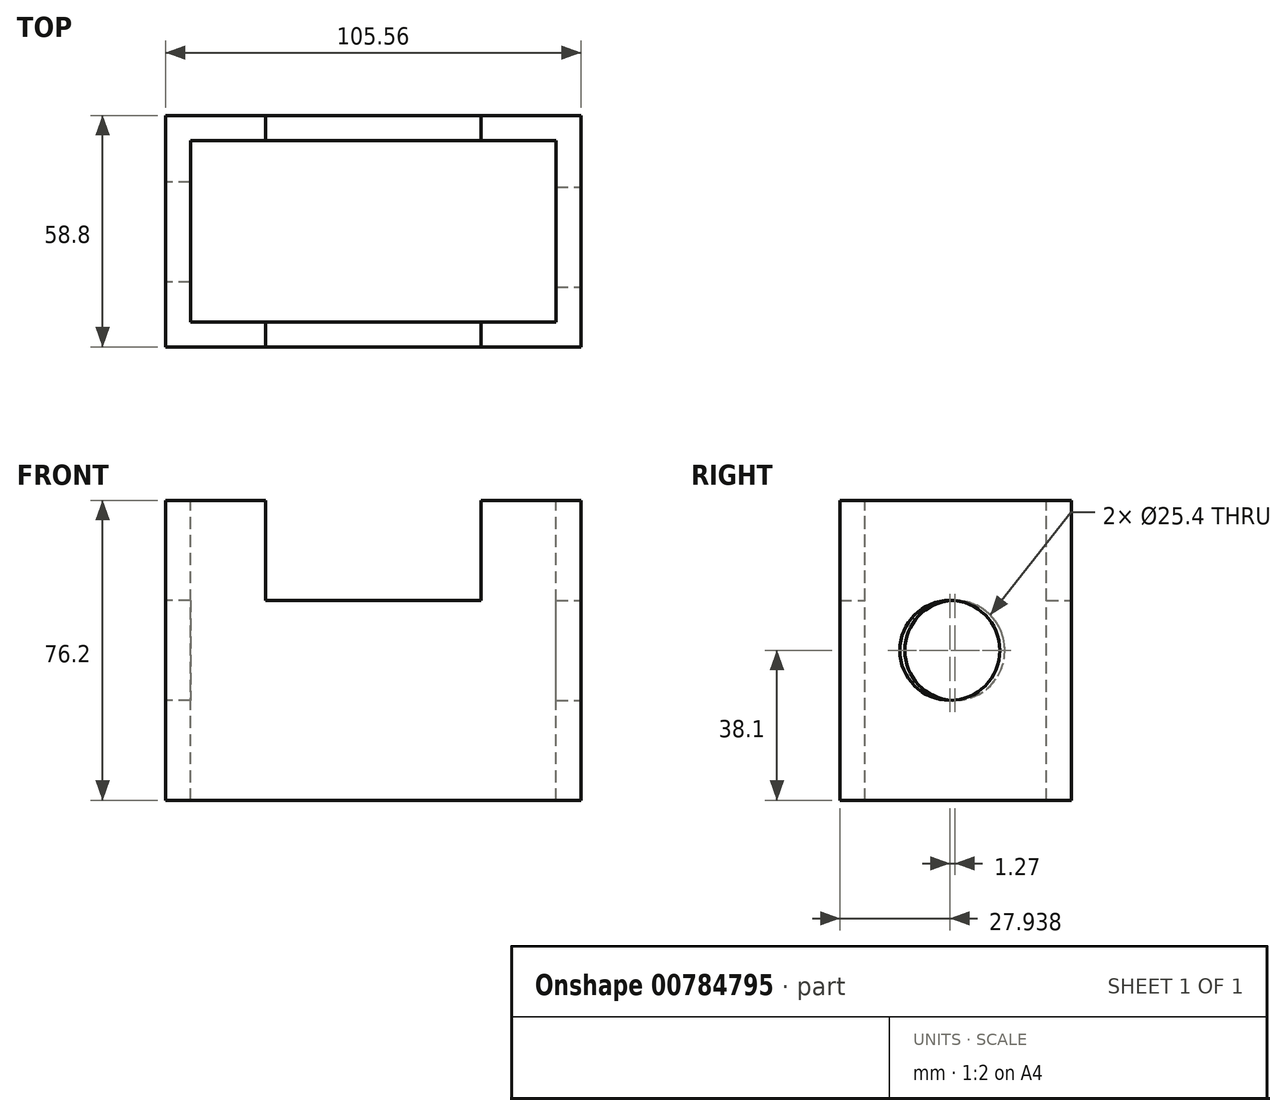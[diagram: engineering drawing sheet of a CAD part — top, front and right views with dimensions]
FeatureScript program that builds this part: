
annotation { "Feature Type Name" : "Feature", "Feature Type Description" : "" }
export const myFeature = defineFeature(function(context is Context, id is Id, definition is map)
    precondition{}
    {
        {
            var Q0;
            Q0=qCreatedBy(makeId("Top.planeOp"),FACE);
            var sketch = newSketch(context, id + "F0", { "sketchPlane" : qUnion([Q0])});
            skLineSegment(sketch, "E0.bottom", {"start": v(-50.25, 19.4) * mm, "end": v(55.3, 19.4) * mm});
            skLineSegment(sketch, "E0.top", {"start": v(-50.25, -39.4) * mm, "end": v(55.3, -39.4) * mm});
            skLineSegment(sketch, "E0.left", {"start": v(-50.25, 19.4) * mm, "end": v(-50.25, -39.4) * mm});
            skLineSegment(sketch, "E0.right", {"start": v(55.3, 19.4) * mm, "end": v(55.3, -39.4) * mm});
            skSolve(sketch);
        }
        {
            var Q0;
            Q0=makeQuery(id+"F0.imprint","IMPRINT",FACE,{"disambiguationData":[TD([[makeQuery(id+"F0.imprint","IMPRINT",EDGE,{"derivedFrom":sQuery(id+"F0.wireOp",EDGE,"E0.bottom")}),-1.0]])]});
            extrude(context, id + "F1", {"entities" : qUnion([Q0]), "depth" : 76.2 * mm, "offsetDistance" : 25.4 * mm});
        }
        {
            var Q0;
            Q0=makeQuery(id+"F1.opExtrude","CAP_FACE",FACE,{"disambiguationData":[OSD([sQuery(id+"F0.wireOp",EDGE,"E0.bottom"),sQuery(id+"F0.wireOp",EDGE,"E0.top"),sQuery(id+"F0.wireOp",EDGE,"E0.left"),sQuery(id+"F0.wireOp",EDGE,"E0.right")])],"isStart":false});
            var sketch = newSketch(context, id + "F2", { "sketchPlane" : qUnion([Q0])});
            skLineSegment(sketch, "E1", {"start": v(-43.9, -33.05) * mm, "end": v(48.96, -33.05) * mm});
            skLineSegment(sketch, "E2", {"start": v(48.96, -33.05) * mm, "end": v(48.96, 13.05) * mm});
            skLineSegment(sketch, "E3", {"start": v(48.96, 13.05) * mm, "end": v(-43.9, 13.05) * mm});
            skLineSegment(sketch, "E4", {"start": v(-43.9, 13.05) * mm, "end": v(-43.9, -33.05) * mm});
            skSolve(sketch);
        }
        {
            var Q0;
            Q0=makeQuery(id+"F2.imprint","IMPRINT",FACE,{"disambiguationData":[TD([[makeQuery(id+"F2.imprint","IMPRINT",EDGE,{"derivedFrom":sQuery(id+"F2.wireOp",EDGE,"E1")}),1.0]])]});
            var Q1;
            Q1=makeQuery(id+"F1.opExtrude","CAP_FACE",FACE,{"disambiguationData":[OSD([sQuery(id+"F0.wireOp",EDGE,"E0.bottom"),sQuery(id+"F0.wireOp",EDGE,"E0.top"),sQuery(id+"F0.wireOp",EDGE,"E0.left"),sQuery(id+"F0.wireOp",EDGE,"E0.right")])],"isStart":true});
            extrude(context, id + "F3", {"entities" : qUnion([Q0]), "operationType" : NewBodyOperationType.REMOVE, "endBound" : BoundingType.UP_TO_SURFACE, "oppositeDirection" : true, "depth" : 25.4 * mm, "endBoundEntityFace" : qUnion([Q1]), "offsetDistance" : 25.4 * mm});
        }
        {
            var Q0;
            Q0=makeQuery(id+"F1.opExtrude","CAP_FACE",FACE,{"disambiguationData":[OSD([sQuery(id+"F0.wireOp",EDGE,"E0.bottom"),sQuery(id+"F0.wireOp",EDGE,"E0.top"),sQuery(id+"F0.wireOp",EDGE,"E0.left"),sQuery(id+"F0.wireOp",EDGE,"E0.right")])],"isStart":false});
            var sketch = newSketch(context, id + "F4", { "sketchPlane" : qUnion([Q0])});
            skLineSegment(sketch, "E5", {"start": v(-24.85, -39.4) * mm, "end": v(-24.85, -33.05) * mm});
            skLineSegment(sketch, "E6", {"start": v(29.9, -39.4) * mm, "end": v(29.9, -33.05) * mm});
            skLineSegment(sketch, "E7", {"start": v(29.9, -33.05) * mm, "end": v(-24.85, -33.05) * mm});
            skLineSegment(sketch, "E8", {"start": v(-24.85, -39.4) * mm, "end": v(29.9, -39.4) * mm});
            skLineSegment(sketch, "E9", {"start": v(-24.85, 13.05) * mm, "end": v(29.9, 13.05) * mm});
            skLineSegment(sketch, "E10", {"start": v(29.9, 13.05) * mm, "end": v(29.9, 19.4) * mm});
            skLineSegment(sketch, "E11", {"start": v(29.9, 19.4) * mm, "end": v(-24.85, 19.4) * mm});
            skLineSegment(sketch, "E12", {"start": v(-24.85, 19.4) * mm, "end": v(-24.85, 13.05) * mm});
            skSolve(sketch);
        }
        {
            var Q0;
            Q0=makeQuery(id+"F4.imprint","IMPRINT",FACE,{"disambiguationData":[TD([[makeQuery(id+"F4.imprint","IMPRINT",EDGE,{"derivedFrom":sQuery(id+"F4.wireOp",EDGE,"E5")}),-1.0]])]});
            var Q1;
            Q1=makeQuery(id+"F4.imprint","IMPRINT",FACE,{"disambiguationData":[TD([[makeQuery(id+"F4.imprint","IMPRINT",EDGE,{"derivedFrom":sQuery(id+"F4.wireOp",EDGE,"E9")}),-1.0]])]});
            extrude(context, id + "F5", {"entities" : qUnion([Q0, Q1]), "operationType" : NewBodyOperationType.REMOVE, "oppositeDirection" : true, "depth" : 25.4 * mm, "offsetDistance" : 25.4 * mm});
        }
        {
            var Q0;
            Q0=makeQuery(id+"F1.opExtrude","SWEPT_FACE",FACE,{"disambiguationData":[OSD([sQuery(id+"F0.wireOp",EDGE,"E0.right")])]});
            var sketch = newSketch(context, id + "F6", { "sketchPlane" : qUnion([Q0])});
            skCircle(sketch, "E13", {"center": v(-11.46, 38.1) * mm, "radius": 12.7 * mm});
            skSolve(sketch);
        }
        {
            var Q0;
            Q0=makeQuery(id+"F6.imprint","IMPRINT",FACE,{"disambiguationData":[TD([[makeQuery(id+"F6.imprint","IMPRINT",EDGE,{"derivedFrom":sQuery(id+"F6.wireOp",EDGE,"E13")}),1.0]])]});
            extrude(context, id + "F7", {"entities" : qUnion([Q0]), "operationType" : NewBodyOperationType.REMOVE, "oppositeDirection" : true, "depth" : 25.4 * mm, "offsetDistance" : 25.4 * mm});
        }
        {
            var Q0;
            Q0=makeQuery(id+"F1.opExtrude","SWEPT_FACE",FACE,{"disambiguationData":[OSD([sQuery(id+"F0.wireOp",EDGE,"E0.left")])]});
            var sketch = newSketch(context, id + "F8", { "sketchPlane" : qUnion([Q0])});
            skCircle(sketch, "E14", {"center": v(10.2, 38.1) * mm, "radius": 12.7 * mm});
            skSolve(sketch);
        }
        {
            var Q0;
            Q0=makeQuery(id+"F8.imprint","IMPRINT",FACE,{"disambiguationData":[TD([[makeQuery(id+"F8.imprint","IMPRINT",EDGE,{"derivedFrom":sQuery(id+"F8.wireOp",EDGE,"E14")}),1.0]])]});
            extrude(context, id + "F9", {"entities" : qUnion([Q0]), "operationType" : NewBodyOperationType.REMOVE, "oppositeDirection" : true, "depth" : 25.4 * mm, "offsetDistance" : 25.4 * mm});
        }
    });
